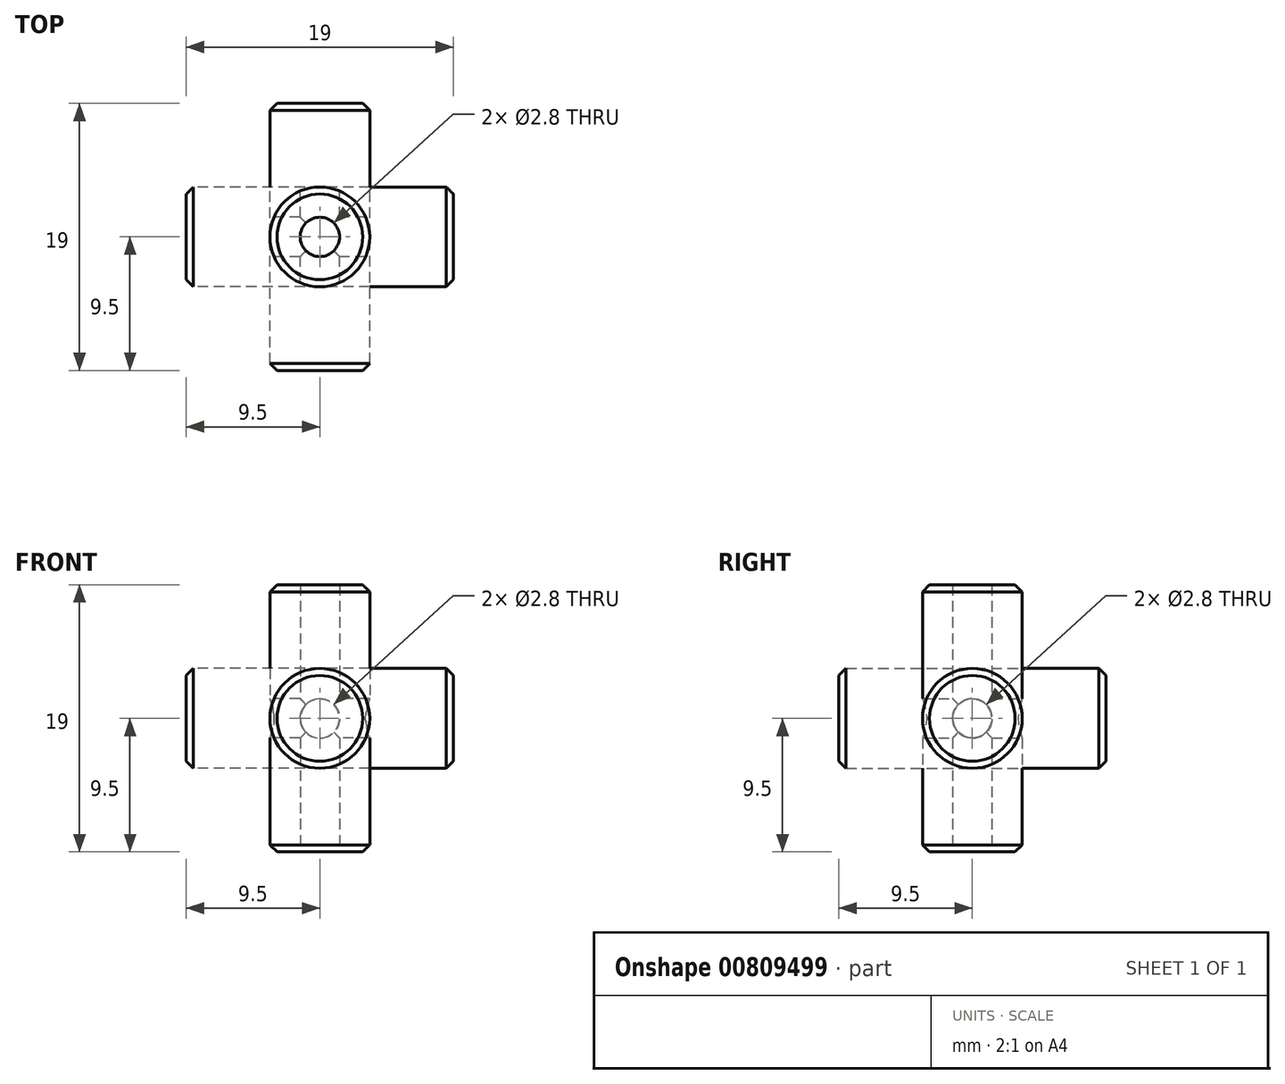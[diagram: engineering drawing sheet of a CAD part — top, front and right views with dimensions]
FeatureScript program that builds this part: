
annotation { "Feature Type Name" : "Feature", "Feature Type Description" : "" }
export const myFeature = defineFeature(function(context is Context, id is Id, definition is map)
    precondition{}
    {
        {
            var Q0;
            Q0=qCreatedBy(makeId("Front.planeOp"),FACE);
            var sketch = newSketch(context, id + "F0", { "sketchPlane" : qUnion([Q0])});
            skCircle(sketch, "E0", {"center": v(0, 0) * mm, "radius": 3.55 * mm});
            skSolve(sketch);
        }
        {
            var Q0;
            Q0 = qSketchRegion(id + "F0", true);
            extrude(context, id + "F1", {"entities" : qUnion([Q0]), "endBound" : BoundingType.SYMMETRIC, "depth" : 19 * mm, "offsetDistance" : 25 * mm});
        }
        {
            var Q0;
            Q0=qCreatedBy(makeId("Front.planeOp"),FACE);
            var sketch = newSketch(context, id + "F2", { "sketchPlane" : qUnion([Q0])});
            skCircle(sketch, "E1", {"center": v(0, 0) * mm, "radius": 1.4 * mm});
            skSolve(sketch);
        }
        {
            var Q0;
            Q0 = qSketchRegion(id + "F2", true);
            extrude(context, id + "F3", {"entities" : qUnion([Q0]), "endBound" : BoundingType.SYMMETRIC, "depth" : 20 * mm, "offsetDistance" : 25 * mm});
        }
        {
            var Q0;
            Q0=qCreatedBy(makeId("Front.planeOp"),FACE);
            var sketch = newSketch(context, id + "F4", { "sketchPlane" : qUnion([Q0])});
            skLineSegment(sketch, "E2.bottom", {"start": v(0, 0) * mm, "end": v(10, 0) * mm});
            skLineSegment(sketch, "E2.top", {"start": v(0, 10) * mm, "end": v(10, 10) * mm});
            skLineSegment(sketch, "E2.left", {"start": v(0, 0) * mm, "end": v(0, 10) * mm});
            skLineSegment(sketch, "E2.right", {"start": v(10, 0) * mm, "end": v(10, 10) * mm});
            skSolve(sketch);
        }
        {
            var Q0;
            Q0=makeQuery(id+"F4.imprint","IMPRINT",FACE,{"disambiguationData":[TD([[makeQuery(id+"F4.imprint","IMPRINT",EDGE,{"derivedFrom":sQuery(id+"F4.wireOp",EDGE,"E2.bottom")}),1.0]])]});
            extrude(context, id + "F5", {"entities" : qUnion([Q0]), "depth" : 10 * mm, "offsetDistance" : 25 * mm});
        }
        {
            var Q0;
            Q0=qCreatedBy(makeId("Origin.pointOp"),VERTEX);
            var Q1;
            Q1=makeQuery(id+"F5.opExtrude","CAP_VERTEX",VERTEX,{"disambiguationData":[OSD([sQuery(id+"F4.wireOp",EDGE,"E2.bottom"),sQuery(id+"F4.wireOp",EDGE,"E2.right")])],"isStart":false});
            var Q2;
            Q2=makeQuery(id+"F5.opExtrude","CAP_VERTEX",VERTEX,{"disambiguationData":[OSD([sQuery(id+"F4.wireOp",EDGE,"E2.top"),sQuery(id+"F4.wireOp",EDGE,"E2.right")])],"isStart":false});
            cPlane(context, id + "F6", {"entities" : qUnion([Q0, Q1, Q2]), "cplaneType" : CPlaneType.THREE_POINT, "offset" : 25 * mm, "width" : 150 * mm, "height" : 150 * mm});
        }
        {
            var Q0;
            Q0=qCreatedBy(id+"F6.planeOp",FACE);
            var sketch = newSketch(context, id + "F7", { "sketchPlane" : qUnion([Q0])});
            skLineSegment(sketch, "E3", {"start": v(0, 0) * mm, "end": v(-14.14, 10) * mm});
            skSolve(sketch);
        }
        {
            var Q0;
            Q0=makeQuery(id+"F5.opExtrude","SWEPT_BODY",BODY,{"disambiguationData":[OSD([sQuery(id+"F4.wireOp",EDGE,"E2.bottom"),sQuery(id+"F4.wireOp",EDGE,"E2.top"),sQuery(id+"F4.wireOp",EDGE,"E2.left"),sQuery(id+"F4.wireOp",EDGE,"E2.right")])]});
            deleteBodies(context, id + "F8", {"entities" : qUnion([Q0])});
        }
        {
            var Q0;
            Q0=makeQuery(id+"F1.opExtrude","SWEPT_BODY",BODY,{"disambiguationData":[OSD([sQuery(id+"F0.wireOp",EDGE,"E0")])]});
            var Q1;
            Q1=makeQuery(id+"F3.opExtrude","SWEPT_BODY",BODY,{"disambiguationData":[OSD([sQuery(id+"F2.wireOp",EDGE,"E1")])]});
            var Q2;
            Q2=sQuery(id+"F7.wireOp",EDGE,"E3");
            circularPattern(context, id + "F9", {"entities" : qUnion([Q0, Q1]), "axis" : qUnion([Q2]), "angle" : 360 * degree, "instanceCount" : 3, "equalSpace" : true});
        }
        {
            var Q0;
            Q0=makeQuery(id+"F9.opPattern","COPY",BODY,{"derivedFrom":makeQuery(id+"F3.opExtrude","SWEPT_BODY",BODY,{"disambiguationData":[OSD([sQuery(id+"F2.wireOp",EDGE,"E1")])]}),"instanceName":"2"});
            var Q1;
            Q1=makeQuery(id+"F9.opPattern","COPY",BODY,{"derivedFrom":makeQuery(id+"F3.opExtrude","SWEPT_BODY",BODY,{"disambiguationData":[OSD([sQuery(id+"F2.wireOp",EDGE,"E1")])]}),"instanceName":"1"});
            var Q2;
            Q2=makeQuery(id+"F3.opExtrude","SWEPT_BODY",BODY,{"disambiguationData":[OSD([sQuery(id+"F2.wireOp",EDGE,"E1")])]});
            var Q3;
            Q3=makeQuery(id+"F9.opPattern","COPY",BODY,{"derivedFrom":makeQuery(id+"F1.opExtrude","SWEPT_BODY",BODY,{"disambiguationData":[OSD([sQuery(id+"F0.wireOp",EDGE,"E0")])]}),"instanceName":"2"});
            booleanBodies(context, id + "F10", {"operationType" : BooleanOperationType.SUBTRACTION, "tools" : qUnion([Q0, Q1, Q2]), "targets" : qUnion([Q3])});
        }
        {
            var Q0;
            Q0=makeQuery(id+"F1.opExtrude","CAP_EDGE",EDGE,{"disambiguationData":[OSD([sQuery(id+"F0.wireOp",EDGE,"E0")])],"isStart":false});
            var Q1;
            Q1=makeQuery(id+"F1.opExtrude","CAP_EDGE",EDGE,{"disambiguationData":[OSD([sQuery(id+"F0.wireOp",EDGE,"E0")])],"isStart":true});
            var Q2;
            Q2=makeQuery(id+"F9.opPattern","COPY",EDGE,{"derivedFrom":makeQuery(id+"F1.opExtrude","CAP_EDGE",EDGE,{"disambiguationData":[OSD([sQuery(id+"F0.wireOp",EDGE,"E0")])],"isStart":false}),"instanceName":"2"});
            var Q3;
            Q3=makeQuery(id+"F9.opPattern","COPY",EDGE,{"derivedFrom":makeQuery(id+"F1.opExtrude","CAP_EDGE",EDGE,{"disambiguationData":[OSD([sQuery(id+"F0.wireOp",EDGE,"E0")])],"isStart":true}),"instanceName":"2"});
            var Q4;
            Q4=makeQuery(id+"F9.opPattern","COPY",EDGE,{"derivedFrom":makeQuery(id+"F1.opExtrude","CAP_EDGE",EDGE,{"disambiguationData":[OSD([sQuery(id+"F0.wireOp",EDGE,"E0")])],"isStart":false}),"instanceName":"1"});
            var Q5;
            Q5=makeQuery(id+"F9.opPattern","COPY",EDGE,{"derivedFrom":makeQuery(id+"F1.opExtrude","CAP_EDGE",EDGE,{"disambiguationData":[OSD([sQuery(id+"F0.wireOp",EDGE,"E0")])],"isStart":true}),"instanceName":"1"});
            chamfer(context, id + "F11", {"entities" : qUnion([Q0, Q1, Q2, Q3, Q4, Q5]), "width" : 0.5 * mm, "tangentPropagation" : true});
        }
    });
